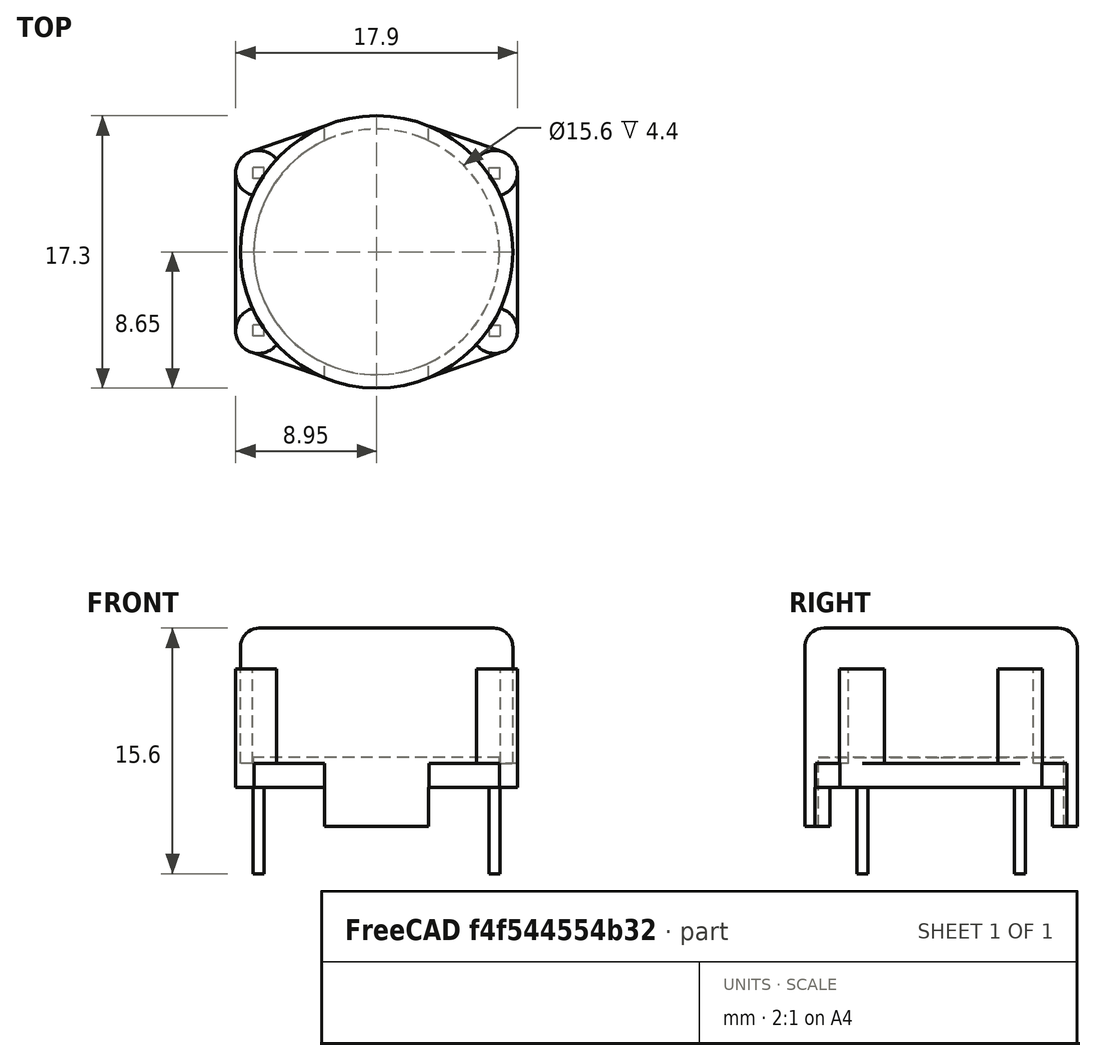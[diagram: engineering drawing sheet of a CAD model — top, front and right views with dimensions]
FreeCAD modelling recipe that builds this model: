
FCSTD DOCUMENT
Label: Drossel_B82721A
objects: Part::Box×7, Part::Cylinder×6, Part::MultiFuse×4, Part::Wedge×4, Part::Fillet×1, Part::Cut×1
note: 23 computed .brp shape members not serialized (recipe doc carries the construction recipe); baked Part::Feature solids carry a one-line shape summary decoded from their .brp

FEATURE [Part::Box] Box  label="Pin"
  Height = 6
  Length = 0.7
  Placement = pos=(7.15,4.65,-3) rot=(0,0,1;0rad)
  Width = 0.7
FEATURE [Part::Box] Box001  label="Pin001"
  Height = 6
  Length = 0.7
  Placement = pos=(7.15,-5.35,-3) rot=(0,0,1;0rad)
  Width = 0.7
FEATURE [Part::Box] Box002  label="Pin002"
  Height = 6
  Length = 0.7
  Placement = pos=(-7.85,4.65,-3) rot=(0,0,1;0rad)
  Width = 0.7
FEATURE [Part::Box] Box003  label="Pin003"
  Height = 6
  Length = 0.7
  Placement = pos=(-7.85,-5.35,-3) rot=(0,0,1;0rad)
  Width = 0.7
FEATURE [Part::MultiFuse] Fusion  label="Pins"
  Shapes = -> [Box,Box001,Box002,Box003]
FEATURE [Part::Cylinder] Cylinder
  Angle = 360
  Height = 12.6
  Radius = 8.65
FEATURE [Part::Cylinder] Cylinder001
  Angle = 360
  Height = 10
  Placement = pos=(7.5,-5,0) rot=(0,0,1;0rad)
  Radius = 1.45
FEATURE [Part::Box] Box004
  Height = 4
  Length = 17.9
  Placement = pos=(-8.95,-5,0) rot=(0,0,1;0rad)
  Width = 10
FEATURE [Part::Wedge] Wedge
  Placement = pos=(0,0,0) rot=(0,0,1;1.5708rad)
  X2max = 6.4
  X2min = 0
  Xmax = 8.1
  Xmin = 0
  Ymax = 7.85
  Ymin = 3
  Z2max = 4
  Z2min = 0
  Zmax = 4
  Zmin = 0
FEATURE [Part::Fillet] Fillet
  Base = -> Cylinder
  Edges = 1 edges r=1.2: [Edge1]
FEATURE [Part::Cylinder] Cylinder001001002  label="Loch_Unterseite"
  Angle = 360
  Height = 4.4
  Radius = 7.8
FEATURE [Part::Cylinder] Cylinder001001003
  Angle = 360
  Height = 10
  Placement = pos=(7.5,5,0) rot=(0,0,1;0rad)
  Radius = 1.45
FEATURE [Part::Cylinder] Cylinder001001004
  Angle = 360
  Height = 10
  Placement = pos=(-7.5,-5,0) rot=(0,0,1;0rad)
  Radius = 1.45
FEATURE [Part::Cylinder] Cylinder001001005
  Angle = 360
  Height = 10
  Placement = pos=(-7.5,5,0) rot=(0,0,1;0rad)
  Radius = 1.45
FEATURE [Part::Wedge] Wedge001
  Placement = pos=(0,0,0) rot=(0,0,1;4.71239rad)
  X2max = 6.4
  X2min = 0
  Xmax = 8.1
  Xmin = 0
  Ymax = 7.85
  Ymin = 3
  Z2max = 4
  Z2min = 0
  Zmax = 4
  Zmin = 0
FEATURE [Part::Wedge] Wedge002
  Placement = pos=(0,0,4) rot=(0.707107,-0.707107,0;3.14159rad)
  X2max = 6.4
  X2min = 0
  Xmax = 8.1
  Xmin = 0
  Ymax = 7.85
  Ymin = 3
  Z2max = 4
  Z2min = 0
  Zmax = 4
  Zmin = 0
FEATURE [Part::Wedge] Wedge003
  Placement = pos=(0,0,4) rot=(0.707107,0.707107,0;3.14159rad)
  X2max = 6.4
  X2min = 0
  Xmax = 8.1
  Xmin = 0
  Ymax = 7.85
  Ymin = 3
  Z2max = 4
  Z2min = 0
  Zmax = 4
  Zmin = 0
FEATURE [Part::MultiFuse] Fusion001  label="Grundkoerper"
  Shapes = -> [Fillet,Cylinder001,Cylinder001001003,Cylinder001001004,Cylinder001001005,Box004,Wedge,Wedge001,Wedge002,Wedge003]
FEATURE [Part::Box] Box005  label="Seitlicher_ausschnitt"
  Height = 2.5
  Length = 10
  Placement = pos=(3.3,-10,0) rot=(0,0,1;0rad)
  Width = 20
FEATURE [Part::Box] Box006  label="Seitlicher_ausschnitt001"
  Height = 2.5
  Length = 10
  Placement = pos=(-3.3,-10,2.5) rot=(0,1,0;3.14159rad)
  Width = 20
FEATURE [Part::MultiFuse] Fusion002  label="Ausschnitte"
  Shapes = -> [Box006,Box005,Cylinder001001002]
FEATURE [Part::Cut] Cut  label="Koerper"
  Base = -> Fusion001
  Tool = -> Fusion002
FEATURE [Part::MultiFuse] Fusion003  label="B82721A"
  Shapes = -> [Fusion,Cut]
